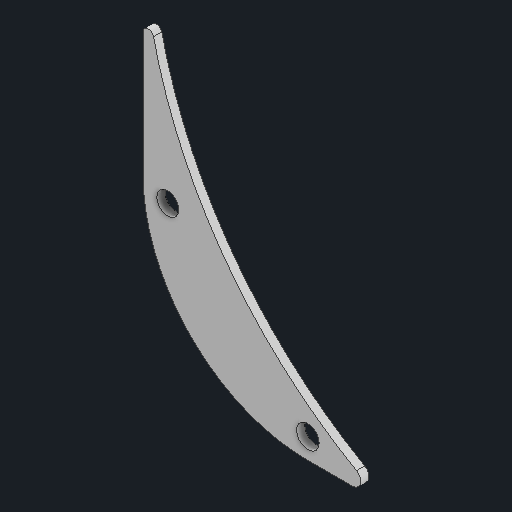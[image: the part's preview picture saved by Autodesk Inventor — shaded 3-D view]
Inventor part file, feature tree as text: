
AUTODESK INVENTOR PART (.ipt)
format: ipt  version: 2025 (Build 290162000, 162)  size: 97,792 bytes
history: native  units: in
note: dims shown in document units (in); Inventor stores cm internally (conversion verified against a paired STEP export)
features: extrude x1, sketch x1
ambient origin geometry x8: Origin, YZ Plane, XZ Plane, XY Plane, X Axis, Y Axis, Z Axis, Center Point
bodies: Solid1 (feature_tree)
feature tree (2):
  extrude  "Extrusion1"  Depth=0.0625in TaperAngle=0.0deg
  sketch  "Sketch1"  dims[d0=0.04in d1=0.0625in d2=1.25in d3=0.0625in d4=0.0in]
